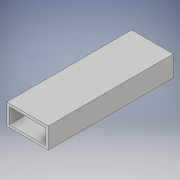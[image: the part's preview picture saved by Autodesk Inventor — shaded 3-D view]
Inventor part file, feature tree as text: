
AUTODESK INVENTOR PART (.ipt)
format: ipt  version: 2019 (Build 230136000, 136)  size: 95,232 bytes
history: native  units: in
note: dims shown in document units (in); Inventor stores cm internally (conversion verified against a paired STEP export)
features: extrude x1, sketch x1
ambient origin geometry x8: Origin, YZ Plane, XZ Plane, XY Plane, X Axis, Y Axis, Z Axis, Center Point
bodies: Solid1 (feature_tree)
feature tree (2):
  extrude  "Extrusion1"  Depth=1.0in
  sketch  "Sketch1"  dims[d0=2.0in d1=1.0in d2=0.125in d3=6.0in d4=0.0in]
